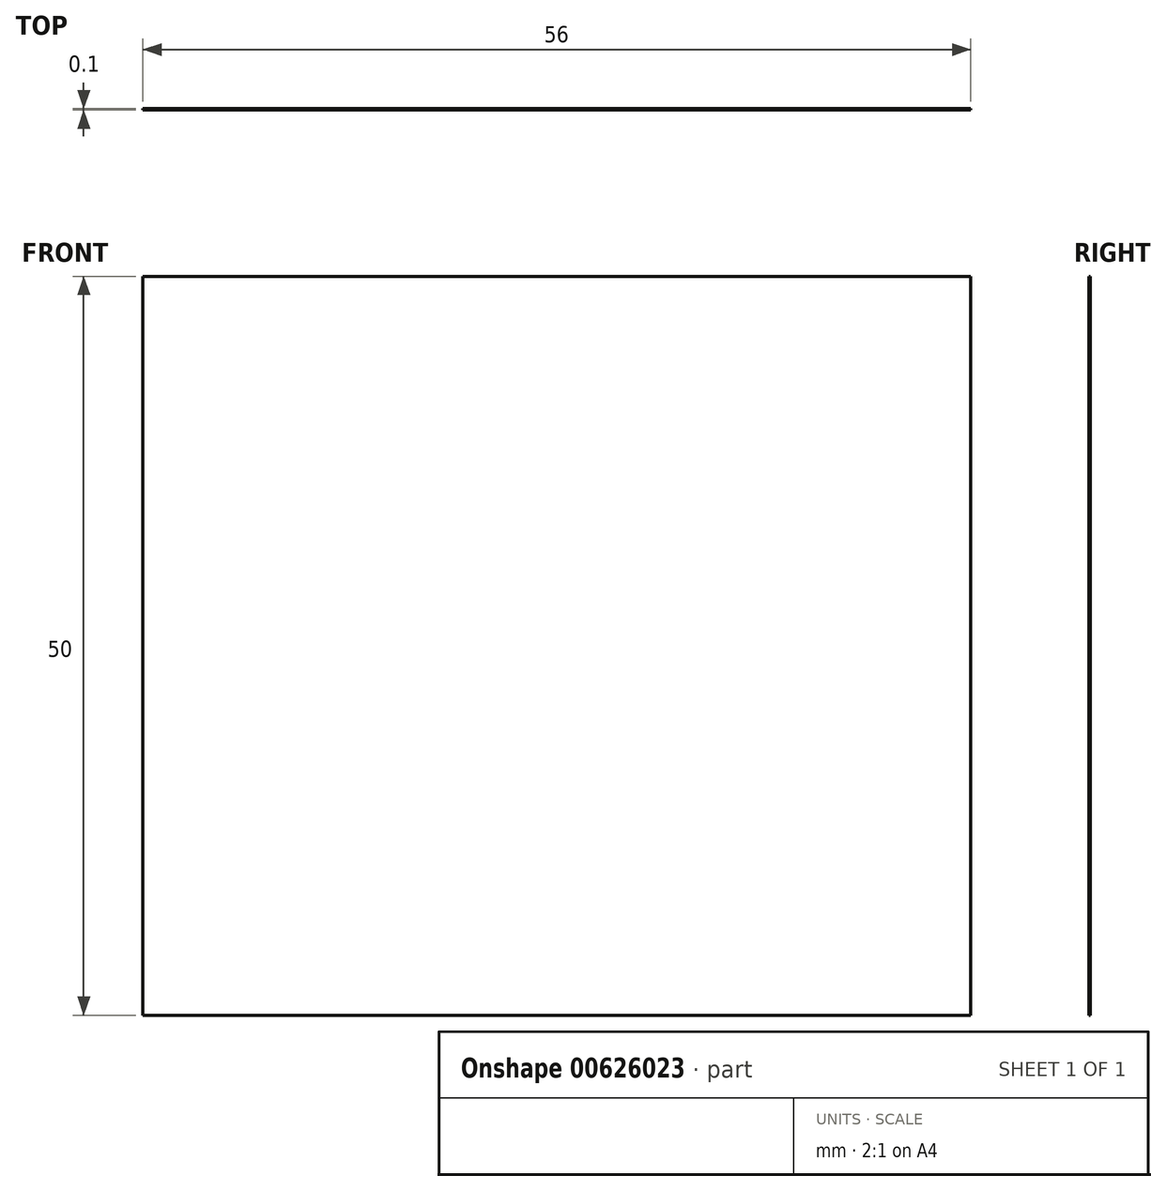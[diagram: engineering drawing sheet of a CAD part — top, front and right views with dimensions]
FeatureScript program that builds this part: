
annotation { "Feature Type Name" : "Feature", "Feature Type Description" : "" }
export const myFeature = defineFeature(function(context is Context, id is Id, definition is map)
    precondition{}
    {
        {
            var Q0;
            Q0=qCreatedBy(makeId("Front.planeOp"),FACE);
            var sketch = newSketch(context, id + "F0", { "sketchPlane" : qUnion([Q0])});
            skLineSegment(sketch, "E0.bottom", {"start": v(28, 25) * mm, "end": v(-28, 25) * mm});
            skLineSegment(sketch, "E0.top", {"start": v(28, -25) * mm, "end": v(-28, -25) * mm});
            skLineSegment(sketch, "E0.left", {"start": v(28, 25) * mm, "end": v(28, -25) * mm});
            skLineSegment(sketch, "E0.right", {"start": v(-28, 25) * mm, "end": v(-28, -25) * mm});
            skPoint(sketch, "E0.middle", {"position": v(0, 0) * mm});
            skSolve(sketch);
        }
        {
            var Q0;
            Q0=makeQuery(id+"F0.imprint","IMPRINT",FACE,{"disambiguationData":[TD([[makeQuery(id+"F0.imprint","IMPRINT",EDGE,{"derivedFrom":sQuery(id+"F0.wireOp",EDGE,"E0.bottom")}),1.0]])]});
            extrude(context, id + "F1", {"entities" : qUnion([Q0]), "depth" : 0.1 * mm, "offsetDistance" : 25 * mm});
        }
    });
